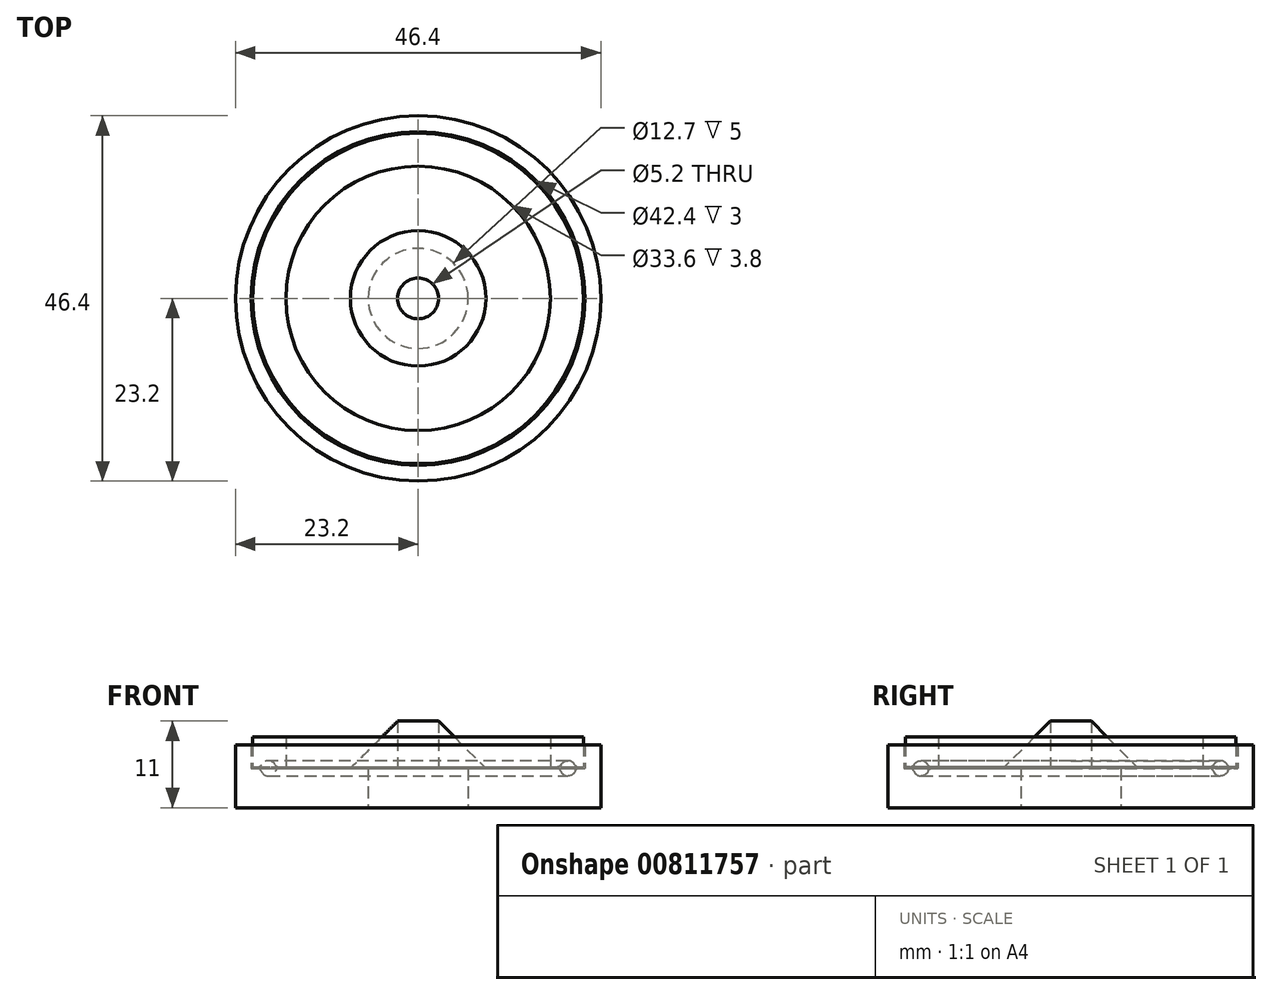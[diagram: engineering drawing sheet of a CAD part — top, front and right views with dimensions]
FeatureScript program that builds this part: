
annotation { "Feature Type Name" : "Feature", "Feature Type Description" : "" }
export const myFeature = defineFeature(function(context is Context, id is Id, definition is map)
    precondition{}
    {
        {
            var Q0;
            Q0=qCreatedBy(makeId("Front.planeOp"),FACE);
            var sketch = newSketch(context, id + "F0", { "sketchPlane" : qUnion([Q0])});
            skLineSegment(sketch, "E0", {"start": v(-6.35, 0) * mm, "end": v(-23.2, 0) * mm});
            skLineSegment(sketch, "E1", {"start": v(-23.2, 0) * mm, "end": v(-23.2, 8) * mm});
            skLineSegment(sketch, "E2", {"start": v(-23.2, 8) * mm, "end": v(-21.2, 8) * mm});
            skLineSegment(sketch, "E3", {"start": v(-21.2, 8) * mm, "end": v(-21.2, 5) * mm});
            skLineSegment(sketch, "E4", {"start": v(-21.2, 5) * mm, "end": v(-20.41, 5) * mm});
            skLineSegment(sketch, "E5", {"start": v(-6.35, 5) * mm, "end": v(-6.35, 0) * mm});
            skLineSegment(sketch, "E6", {"start": v(-6.35, 5) * mm, "end": v(-2.6, 5) * mm});
            skLineSegment(sketch, "E7", {"start": v(-2.6, 5) * mm, "end": v(-2.6, 11) * mm});
            skLineSegment(sketch, "E8", {"start": v(-2.6, 11) * mm, "end": v(-8.6, 5) * mm});
            skLineSegment(sketch, "E9", {"start": v(0, 0) * mm, "end": v(0, 17.83) * mm, "construction": true});
            skArc(sketch, "E10", {"start": v(-18.17, 5.46) * mm, "mid": v(-19.02, 5.97) * mm, "end": v(-19.88, 5.46) * mm});
            skLineSegment(sketch, "E11", {"start": v(-16.8, 5.2) * mm, "end": v(-17.73, 5.2) * mm});
            skLineSegment(sketch, "E12", {"start": v(-21, 5.2) * mm, "end": v(-21, 9) * mm});
            skLineSegment(sketch, "E13", {"start": v(-21, 9) * mm, "end": v(-16.8, 9) * mm});
            skLineSegment(sketch, "E14", {"start": v(-16.8, 9) * mm, "end": v(-16.8, 5.2) * mm});
            skArc(sketch, "E15.trimOffspring", {"start": v(-19.94, 4.67) * mm, "mid": v(-19.02, 4.02) * mm, "end": v(-18.1, 4.67) * mm});
            skLineSegment(sketch, "E16.trimOffspring", {"start": v(-17.64, 5) * mm, "end": v(-8.6, 5) * mm});
            skLineSegment(sketch, "E17.trimOffspring", {"start": v(-20.32, 5.2) * mm, "end": v(-21, 5.2) * mm});
            skPoint(sketch, "E18.visualSharp", {"position": v(-18.07, 5.2) * mm});
            skArc(sketch, "E18.filletArc", {"start": v(-18.17, 5.46) * mm, "mid": v(-17.98, 5.27) * mm, "end": v(-17.73, 5.2) * mm});
            skPoint(sketch, "E19.visualSharp", {"position": v(-19.98, 5.2) * mm});
            skArc(sketch, "E19.filletArc", {"start": v(-20.32, 5.2) * mm, "mid": v(-20.07, 5.27) * mm, "end": v(-19.88, 5.46) * mm});
            skPoint(sketch, "E20.visualSharp", {"position": v(-20, 5) * mm});
            skArc(sketch, "E20.filletArc", {"start": v(-19.94, 4.67) * mm, "mid": v(-20.13, 4.9) * mm, "end": v(-20.41, 5) * mm});
            skPoint(sketch, "E21.visualSharp", {"position": v(-18.05, 5) * mm});
            skArc(sketch, "E21.filletArc", {"start": v(-17.64, 5) * mm, "mid": v(-17.92, 4.9) * mm, "end": v(-18.1, 4.67) * mm});
            skSolve(sketch);
        }
        {
            var Q0;
            Q0=makeQuery(id+"F0.imprint","IMPRINT",FACE,{"disambiguationData":[TD([[makeQuery(id+"F0.imprint","IMPRINT",EDGE,{"derivedFrom":sQuery(id+"F0.wireOp",EDGE,"E0")}),-1.0]])]});
            var Q1;
            {var subQ0=sQuery(id+"F0.wireOp",EDGE,"E6");Q1=makeQuery(id+"F0.imprint","IMPRINT",FACE,{"disambiguationData":[TD([[makeQuery(id+"F0.imprint","IMPRINT",EDGE,{"derivedFrom":subQ0}),1.0]])]});}
            var Q2;
            {var subQ0=sQuery(id+"F0.wireOp",EDGE,"E12");Q2=makeQuery(id+"F0.imprint","IMPRINT",FACE,{"disambiguationData":[TD([[makeQuery(id+"F0.imprint","IMPRINT",EDGE,{"derivedFrom":subQ0}),-1.0]])]});}
            var Q3;
            Q3=sQuery(id+"F0.wireOp",EDGE,"E9");
            revolve(context, id + "F1", {"surfaceOperationType" : NewSurfaceOperationType.NEW, "entities" : qUnion([Q0, Q1, Q2]), "axis" : qUnion([Q3]), "revolveType" : RevolveType.FULL});
        }
    });
